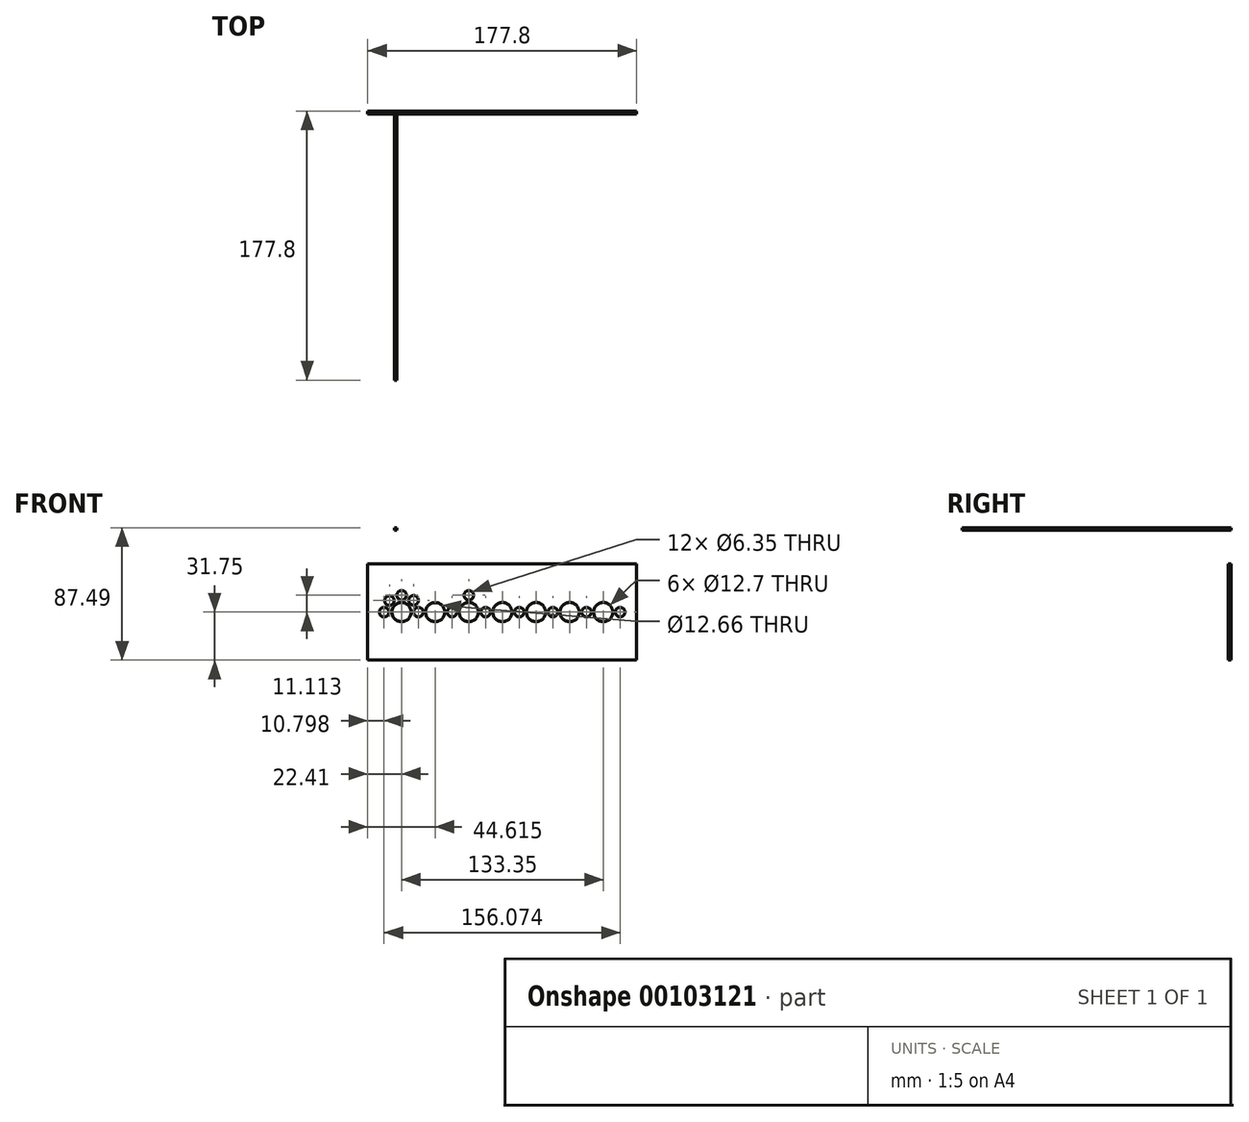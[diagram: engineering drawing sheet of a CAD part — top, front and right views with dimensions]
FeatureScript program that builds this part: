
annotation { "Feature Type Name" : "Feature", "Feature Type Description" : "" }
export const myFeature = defineFeature(function(context is Context, id is Id, definition is map)
    precondition{}
    {
        {
            var Q0;
            Q0=qCreatedBy(makeId("Front.planeOp"),FACE);
            var sketch = newSketch(context, id + "F0", { "sketchPlane" : qUnion([Q0])});
            skLineSegment(sketch, "E0.bottom", {"start": v(88.9, -31.75) * mm, "end": v(-88.9, -31.75) * mm});
            skLineSegment(sketch, "E0.top", {"start": v(88.9, 31.75) * mm, "end": v(-88.9, 31.75) * mm});
            skLineSegment(sketch, "E0.left", {"start": v(88.9, -31.75) * mm, "end": v(88.9, 31.75) * mm});
            skLineSegment(sketch, "E0.right", {"start": v(-88.9, -31.75) * mm, "end": v(-88.9, 31.75) * mm});
            skPoint(sketch, "E0.middle", {"position": v(0, 0) * mm});
            skLineSegment(sketch, "E1", {"start": v(-88.9, 0) * mm, "end": v(-82.55, 0) * mm});
            skPoint(sketch, "E1.endSnap0", {"position": v(-88.9, 0) * mm});
            skCircle(sketch, "E2", {"center": v(-78.1, 0) * mm, "radius": 3.18 * mm});
            skCircle(sketch, "E3", {"center": v(-66.49, 0) * mm, "radius": 6.35 * mm});
            skLineSegment(sketch, "E4", {"start": v(-74.93, 0) * mm, "end": v(-73.34, 0) * mm});
            skLineSegment(sketch, "E5", {"start": v(-60.14, 0) * mm, "end": v(-58.55, 0) * mm});
            skCircle(sketch, "E6", {"center": v(-55.38, 0) * mm, "radius": 3.18 * mm});
            skLineSegment(sketch, "E7", {"start": v(-52.2, 0) * mm, "end": v(-50.61, 0) * mm});
            skCircle(sketch, "E8", {"center": v(-44.29, 0) * mm, "radius": 6.33 * mm});
            skLineSegment(sketch, "E9", {"start": v(-37.96, 0) * mm, "end": v(-36.33, 0) * mm});
            skCircle(sketch, "E10", {"center": v(-33.15, 0) * mm, "radius": 3.18 * mm});
            skLineSegment(sketch, "E11", {"start": v(-29.98, 0) * mm, "end": v(-28.39, 0) * mm});
            skCircle(sketch, "E12", {"center": v(-22.04, 0) * mm, "radius": 6.35 * mm});
            skLineSegment(sketch, "E13", {"start": v(-15.69, 0) * mm, "end": v(-14.1, 0) * mm});
            skCircle(sketch, "E14", {"center": v(-10.93, 0) * mm, "radius": 3.18 * mm});
            skLineSegment(sketch, "E15", {"start": v(-7.75, 0) * mm, "end": v(-6.16, 0) * mm});
            skCircle(sketch, "E16", {"center": v(0.19, 0) * mm, "radius": 6.35 * mm});
            skLineSegment(sketch, "E17", {"start": v(6.54, 0) * mm, "end": v(8.12, 0) * mm});
            skCircle(sketch, "E18", {"center": v(11.3, 0) * mm, "radius": 3.18 * mm});
            skLineSegment(sketch, "E19", {"start": v(14.47, 0) * mm, "end": v(16.06, 0) * mm});
            skCircle(sketch, "E20", {"center": v(22.41, 0) * mm, "radius": 6.35 * mm});
            skLineSegment(sketch, "E21", {"start": v(28.76, 0) * mm, "end": v(30.35, 0) * mm});
            skCircle(sketch, "E22", {"center": v(33.52, 0) * mm, "radius": 3.18 * mm});
            skLineSegment(sketch, "E23", {"start": v(36.7, 0) * mm, "end": v(38.29, 0) * mm});
            skCircle(sketch, "E24", {"center": v(44.64, 0) * mm, "radius": 6.35 * mm});
            skLineSegment(sketch, "E25", {"start": v(50.99, 0) * mm, "end": v(52.57, 0) * mm});
            skCircle(sketch, "E26", {"center": v(55.75, 0) * mm, "radius": 3.18 * mm});
            skLineSegment(sketch, "E27", {"start": v(58.92, 0) * mm, "end": v(60.51, 0) * mm});
            skCircle(sketch, "E28", {"center": v(66.86, 0) * mm, "radius": 6.35 * mm});
            skLineSegment(sketch, "E29", {"start": v(73.21, 0) * mm, "end": v(74.8, 0) * mm});
            skCircle(sketch, "E30", {"center": v(77.97, 0) * mm, "radius": 3.18 * mm});
            skLineSegment(sketch, "E31", {"start": v(-66.49, 6.35) * mm, "end": v(-66.49, 7.94) * mm});
            skCircle(sketch, "E32", {"center": v(-66.48, 11.11) * mm, "radius": 3.18 * mm});
            skLineSegment(sketch, "E33", {"start": v(-71.08, 4.4) * mm, "end": v(-72.39, 5.29) * mm});
            skCircle(sketch, "E34", {"center": v(-74.54, 7.62) * mm, "radius": 3.18 * mm});
            skLineSegment(sketch, "E35", {"start": v(-61.98, 4.47) * mm, "end": v(-60.8, 5.53) * mm});
            skCircle(sketch, "E36", {"center": v(-58.58, 7.8) * mm, "radius": 3.18 * mm});
            skLineSegment(sketch, "E37", {"start": v(-22.04, 6.35) * mm, "end": v(-22.04, 7.94) * mm});
            skCircle(sketch, "E38", {"center": v(-22.04, 11.11) * mm, "radius": 3.18 * mm});
            skLineSegment(sketch, "E39", {"start": v(0.19, 6.35) * mm, "end": v(0.19, 22.48) * mm});
            skSolve(sketch);
        }
        {
            var Q0;
            Q0=makeQuery(id+"F0.imprint","IMPRINT",FACE,{"disambiguationData":[TD([[makeQuery(id+"F0.imprint","IMPRINT",EDGE,{"derivedFrom":sQuery(id+"F0.wireOp",EDGE,"E0.bottom")}),-1.0]])]});
            extrude(context, id + "F1", {"entities" : qUnion([Q0]), "depth" : 2 * mm});
        }
        {
            var Q0;
            Q0=qCreatedBy(makeId("Front.planeOp"),FACE);
            var sketch = newSketch(context, id + "F2", { "sketchPlane" : qUnion([Q0])});
            skLineSegment(sketch, "E40.bottom", {"start": v(-69.72, 54.16) * mm, "end": v(-71.3, 54.16) * mm});
            skLineSegment(sketch, "E40.top", {"start": v(-69.72, 55.74) * mm, "end": v(-71.3, 55.74) * mm});
            skLineSegment(sketch, "E40.left", {"start": v(-69.72, 54.16) * mm, "end": v(-69.72, 55.74) * mm});
            skLineSegment(sketch, "E40.right", {"start": v(-71.3, 54.16) * mm, "end": v(-71.3, 55.74) * mm});
            skPoint(sketch, "E40.middle", {"position": v(-70.51, 54.95) * mm});
            skSolve(sketch);
        }
        {
            var Q0;
            Q0 = qSketchRegion(id + "F2", true);
            extrude(context, id + "F3", {"entities" : qUnion([Q0]), "depth" : 177.8 * mm});
        }
    });
